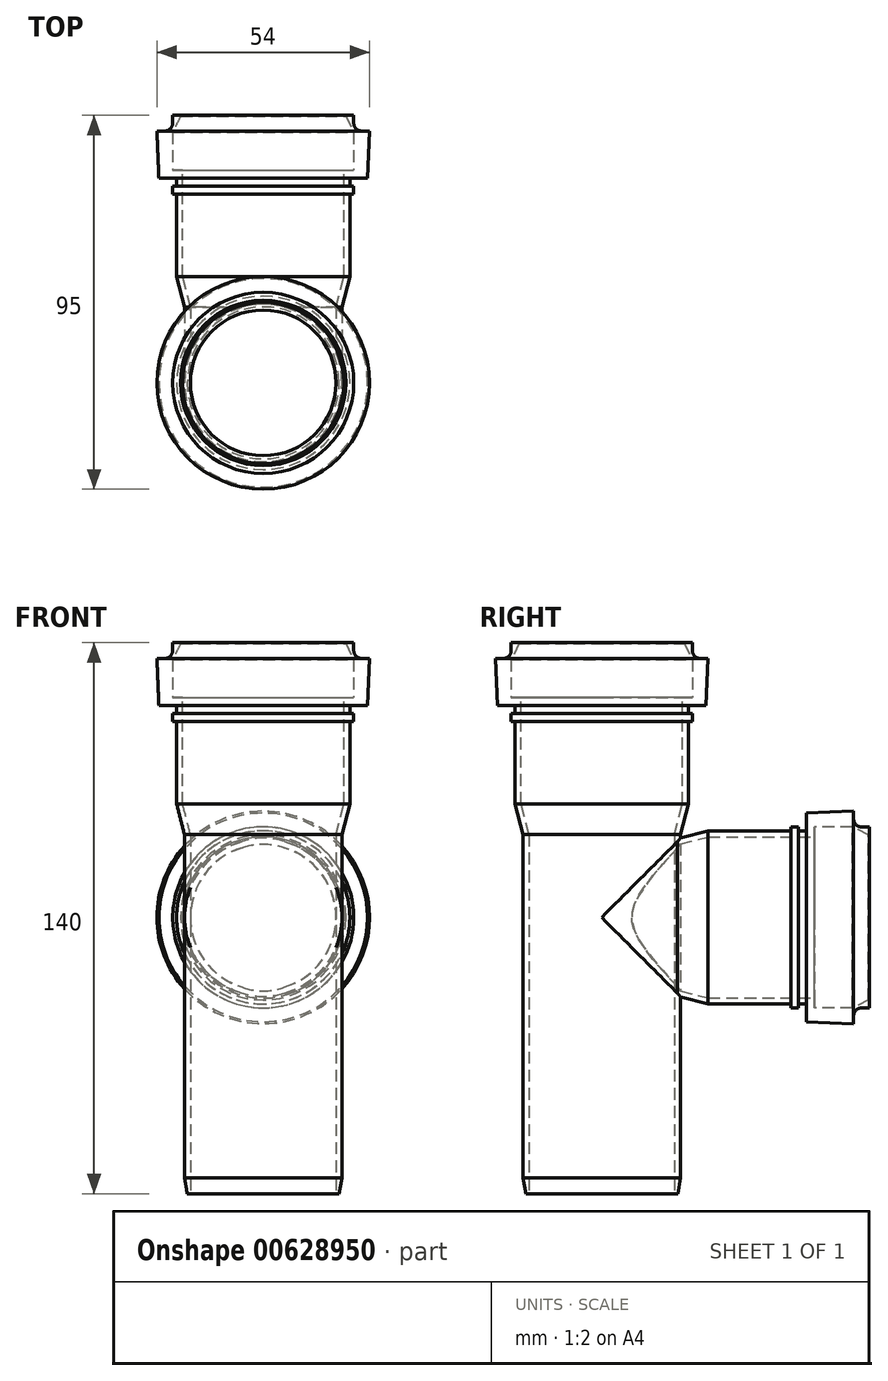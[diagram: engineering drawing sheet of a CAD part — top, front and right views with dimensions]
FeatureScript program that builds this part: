
annotation { "Feature Type Name" : "Feature", "Feature Type Description" : "" }
export const myFeature = defineFeature(function(context is Context, id is Id, definition is map)
    precondition{}
    {
        {
            var Q0;
            Q0=qCreatedBy(makeId("Front.planeOp"),FACE);
            var sketch = newSketch(context, id + "F0", { "sketchPlane" : qUnion([Q0])});
            skLineSegment(sketch, "E0", {"start": v(21.37, -67.8) * mm, "end": v(21.37, 7.5) * mm});
            skLineSegment(sketch, "E1", {"start": v(-0.63, -1.77) * mm, "end": v(-0.63, -22.77) * mm});
            skLineSegment(sketch, "E2", {"start": v(-0.63, -22.77) * mm, "end": v(1.37, -30.52) * mm});
            skLineSegment(sketch, "E3", {"start": v(-0.63, -1.77) * mm, "end": v(-1.63, -1.77) * mm});
            skLineSegment(sketch, "E4", {"start": v(-1.63, -1.77) * mm, "end": v(-1.63, 0.23) * mm});
            skLineSegment(sketch, "E5", {"start": v(-1.63, 0.23) * mm, "end": v(-0.63, 0.23) * mm});
            skLineSegment(sketch, "E6", {"start": v(-0.63, 0.23) * mm, "end": v(-0.63, 2.23) * mm});
            skLineSegment(sketch, "E7", {"start": v(-0.63, 2.23) * mm, "end": v(-5.13, 2.23) * mm});
            skLineSegment(sketch, "E8", {"start": v(-5.13, 2.23) * mm, "end": v(-5.63, 14.22) * mm});
            skLineSegment(sketch, "E9", {"start": v(-5.63, 14.22) * mm, "end": v(-3.63, 14.22) * mm});
            skLineSegment(sketch, "E10", {"start": v(-1.63, 16.22) * mm, "end": v(-1.63, 18.22) * mm});
            skLineSegment(sketch, "E11", {"start": v(-1.63, 18.22) * mm, "end": v(0.37, 18.22) * mm});
            skLineSegment(sketch, "E12", {"start": v(-1.63, 4.23) * mm, "end": v(-1.63, 13.9) * mm});
            skLineSegment(sketch, "E13", {"start": v(-1.63, 4.23) * mm, "end": v(0.87, 4.24) * mm});
            skPoint(sketch, "E14.visualSharp", {"position": v(-1.63, 14.22) * mm});
            skArc(sketch, "E14.filletArc", {"start": v(-3.63, 14.22) * mm, "mid": v(-2.22, 14.8) * mm, "end": v(-1.63, 16.22) * mm});
            skLineSegment(sketch, "E15", {"start": v(1.37, -30.52) * mm, "end": v(2.87, -30.52) * mm});
            skLineSegment(sketch, "E16", {"start": v(0.89, -22.73) * mm, "end": v(0.87, 4.24) * mm});
            skLineSegment(sketch, "E17", {"start": v(2.87, -30.52) * mm, "end": v(0.89, -22.73) * mm});
            skLineSegment(sketch, "E18", {"start": v(0.37, 18.22) * mm, "end": v(0.37, 17.95) * mm});
            skLineSegment(sketch, "E19", {"start": v(0.37, 17.95) * mm, "end": v(-1.63, 13.9) * mm});
            skLineSegment(sketch, "E20", {"start": v(2.87, -30.52) * mm, "end": v(2.87, -36.78) * mm});
            skLineSegment(sketch, "E21", {"start": v(2.87, -36.78) * mm, "end": v(1.37, -36.78) * mm});
            skLineSegment(sketch, "E22", {"start": v(1.37, -36.78) * mm, "end": v(1.37, -30.52) * mm});
            skSolve(sketch);
        }
        {
            var Q0;
            Q0=makeQuery(id+"F0.imprint","IMPRINT",FACE,{"disambiguationData":[TD([[makeQuery(id+"F0.imprint","IMPRINT",EDGE,{"derivedFrom":sQuery(id+"F0.wireOp",EDGE,"E1")}),1.0]])]});
            var Q1;
            Q1=makeQuery(id+"F0.imprint","IMPRINT",FACE,{"disambiguationData":[TD([[makeQuery(id+"F0.imprint","IMPRINT",EDGE,{"derivedFrom":sQuery(id+"F0.wireOp",EDGE,"E15")}),-1.0]])]});
            var Q2;
            Q2=sQuery(id+"F0.wireOp",EDGE,"E0");
            revolve(context, id + "F1", {"entities" : qUnion([Q0, Q1]), "axis" : qUnion([Q2]), "revolveType" : RevolveType.FULL});
        }
        {
            var Q0;
            Q0=makeQuery(id+"F1.opRevolve","SWEPT_FACE",FACE,{"disambiguationData":[OSD([sQuery(id+"F0.wireOp",EDGE,"E21")])]});
            extrude(context, id + "F2", {"entities" : qUnion([Q0]), "depth" : (90 - 5) * mm, "offsetDistance" : 25 * mm});
        }
        {
            var Q0;
            Q0=makeQuery(id+"F1.opRevolve","SWEPT_BODY",BODY,{"disambiguationData":[OSD([sQuery(id+"F0.wireOp",EDGE,"E1"),sQuery(id+"F0.wireOp",EDGE,"E2"),sQuery(id+"F0.wireOp",EDGE,"E3"),sQuery(id+"F0.wireOp",EDGE,"E4"),sQuery(id+"F0.wireOp",EDGE,"E5"),sQuery(id+"F0.wireOp",EDGE,"E6"),sQuery(id+"F0.wireOp",EDGE,"E7"),sQuery(id+"F0.wireOp",EDGE,"E8"),sQuery(id+"F0.wireOp",EDGE,"E9"),sQuery(id+"F0.wireOp",EDGE,"E10"),sQuery(id+"F0.wireOp",EDGE,"E11"),sQuery(id+"F0.wireOp",EDGE,"E12"),sQuery(id+"F0.wireOp",EDGE,"E13"),sQuery(id+"F0.wireOp",EDGE,"E14.filletArc"),sQuery(id+"F0.wireOp",EDGE,"E16"),sQuery(id+"F0.wireOp",EDGE,"E17"),sQuery(id+"F0.wireOp",EDGE,"E18"),sQuery(id+"F0.wireOp",EDGE,"E19"),sQuery(id+"F0.wireOp",EDGE,"E20"),sQuery(id+"F0.wireOp",EDGE,"E21"),sQuery(id+"F0.wireOp",EDGE,"E22")])]});
            var Q1;
            Q1=sQuery(id+"F0.wireOp",EDGE,"E7");
            transform(context, id + "F3", {"entities" : qUnion([Q0]), "transformType" : TransformType.ROTATION, "transformAxis" : qUnion([Q1]), "angle" : 90 * degree, "makeCopy" : true});
        }
        {
            var Q0;
            Q0=makeQuery(id+"F3.opPattern","COPY",BODY,{"derivedFrom":makeQuery(id+"F1.opRevolve","SWEPT_BODY",BODY,{"disambiguationData":[OSD([sQuery(id+"F0.wireOp",EDGE,"E1"),sQuery(id+"F0.wireOp",EDGE,"E2"),sQuery(id+"F0.wireOp",EDGE,"E3"),sQuery(id+"F0.wireOp",EDGE,"E4"),sQuery(id+"F0.wireOp",EDGE,"E5"),sQuery(id+"F0.wireOp",EDGE,"E6"),sQuery(id+"F0.wireOp",EDGE,"E7"),sQuery(id+"F0.wireOp",EDGE,"E8"),sQuery(id+"F0.wireOp",EDGE,"E9"),sQuery(id+"F0.wireOp",EDGE,"E10"),sQuery(id+"F0.wireOp",EDGE,"E11"),sQuery(id+"F0.wireOp",EDGE,"E12"),sQuery(id+"F0.wireOp",EDGE,"E13"),sQuery(id+"F0.wireOp",EDGE,"E14.filletArc"),sQuery(id+"F0.wireOp",EDGE,"E16"),sQuery(id+"F0.wireOp",EDGE,"E17"),sQuery(id+"F0.wireOp",EDGE,"E18"),sQuery(id+"F0.wireOp",EDGE,"E19"),sQuery(id+"F0.wireOp",EDGE,"E20"),sQuery(id+"F0.wireOp",EDGE,"E21"),sQuery(id+"F0.wireOp",EDGE,"E22")])]}),"instanceName":"1"});
            transform(context, id + "F4", {"entities" : qUnion([Q0]), "transformType" : TransformType.TRANSLATION_3D, "dx" : 0 * mm, "dy" : (52.8 - 0.79) * mm, "dz" : (-54.1 + 0.28) * mm, "makeCopy" : false});
        }
        {
            var Q0;
            Q0=makeQuery(id+"F3.opPattern","COPY",FACE,{"derivedFrom":makeQuery(id+"F1.opRevolve","SWEPT_FACE",FACE,{"disambiguationData":[OSD([sQuery(id+"F0.wireOp",EDGE,"E21")])]}),"instanceName":"1"});
            extrude(context, id + "F5", {"entities" : qUnion([Q0]), "operationType" : NewBodyOperationType.ADD, "depth" : 13 * mm, "offsetDistance" : 25 * mm});
        }
        {
            var Q0;
            Q0=makeQuery(id+"F2.opExtrude","CAP_FACE",FACE,{"disambiguationData":[OSD([sQuery(id+"F0.wireOp",EDGE,"E21")])],"isStart":false});
            var sketch = newSketch(context, id + "F6", { "sketchPlane" : qUnion([Q0])});
            skSolve(sketch);
        }
        {
            var Q0;
            Q0=makeQuery(id+"F6.imprint","IMPRINT",FACE,{"disambiguationData":[TD([[makeQuery(id+"F6.imprint","IMPRINT",EDGE,{"derivedFrom":makeQuery(id+"F2.opExtrude","CAP_EDGE",EDGE,{"disambiguationData":[OSD([sQuery(id+"F0.wireOp",EDGE,"E20"),sQuery(id+"F0.wireOp",EDGE,"E21")])],"isStart":false})}),1.0]])]});
            extrude(context, id + "F7", {"entities" : qUnion([Q0]), "operationType" : NewBodyOperationType.REMOVE, "oppositeDirection" : true, "depth" : 93.4 * mm, "offsetDistance" : 25 * mm});
        }
        {
            var Q0;
            Q0=makeQuery(id+"F2.opExtrude","CAP_EDGE",EDGE,{"disambiguationData":[OSD([sQuery(id+"F0.wireOp",EDGE,"E21"),sQuery(id+"F0.wireOp",EDGE,"E22")])],"isStart":false});
            chamfer(context, id + "F8", {"entities" : qUnion([Q0]), "chamferType" : ChamferType.OFFSET_ANGLE, "width" : 4 * mm, "oppositeDirection" : true, "angle" : 10 * degree, "tangentPropagation" : true});
        }
    });
